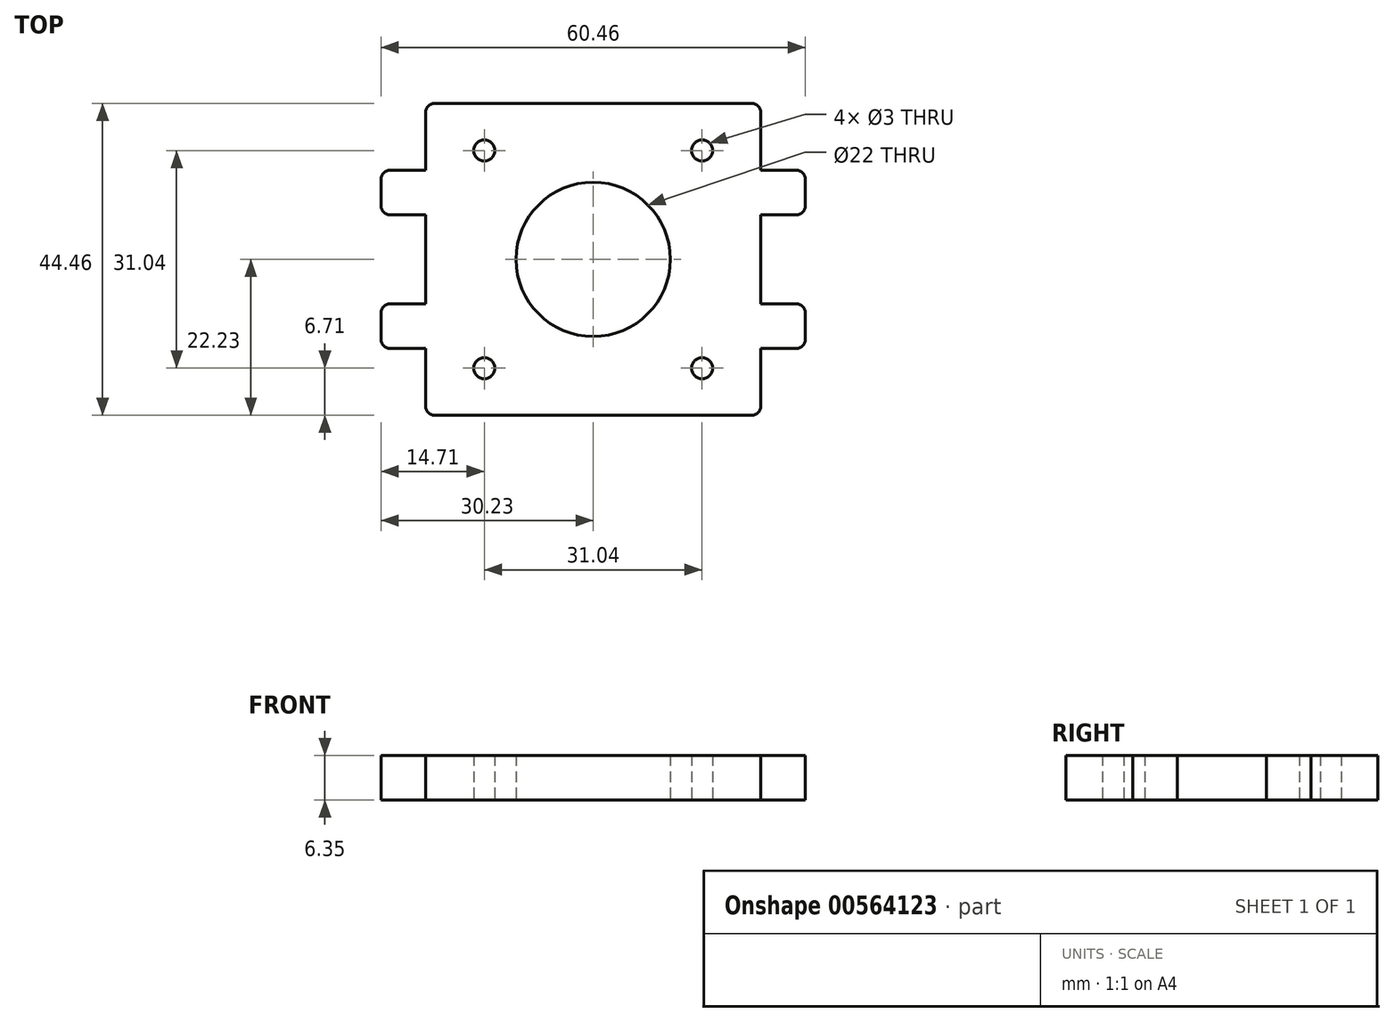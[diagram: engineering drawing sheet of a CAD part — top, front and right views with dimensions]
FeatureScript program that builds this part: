
annotation { "Feature Type Name" : "Feature", "Feature Type Description" : "" }
export const myFeature = defineFeature(function(context is Context, id is Id, definition is map)
    precondition{}
    {
        {
            var Q0;
            Q0=qCreatedBy(makeId("Top.planeOp"),FACE);
            var sketch = newSketch(context, id + "F0", { "sketchPlane" : qUnion([Q0])});
            skLineSegment(sketch, "E0.bottom", {"start": v(-23.88, 22.22) * mm, "end": v(23.88, 22.23) * mm});
            skLineSegment(sketch, "E0.top", {"start": v(-23.88, -22.23) * mm, "end": v(23.88, -22.22) * mm});
            skLineSegment(sketch, "E0.left", {"start": v(-23.88, 22.22) * mm, "end": v(-23.88, -22.23) * mm});
            skLineSegment(sketch, "E0.right", {"start": v(23.88, 22.23) * mm, "end": v(23.88, -22.22) * mm});
            skPoint(sketch, "E0.middle", {"position": v(0, 0) * mm});
            skLineSegment(sketch, "E1", {"start": v(0, 5.5) * mm, "end": v(0, -5.9) * mm});
            skLineSegment(sketch, "E2", {"start": v(-5.75, 0) * mm, "end": v(7.69, 0) * mm});
            skCircle(sketch, "E3", {"center": v(-15.52, 15.52) * mm, "radius": 1.5 * mm});
            skCircle(sketch, "E4.MirrorC", {"center": v(15.52, 15.52) * mm, "radius": 1.5 * mm});
            skCircle(sketch, "E5.MirrorC", {"center": v(-15.52, -15.52) * mm, "radius": 1.5 * mm});
            skCircle(sketch, "E6.MirrorC", {"center": v(15.52, -15.52) * mm, "radius": 1.5 * mm});
            skCircle(sketch, "E7", {"center": v(0, 0) * mm, "radius": 11 * mm});
            skLineSegment(sketch, "E8", {"start": v(-23.88, 12.7) * mm, "end": v(-30.23, 12.7) * mm});
            skLineSegment(sketch, "E9", {"start": v(-30.23, 12.7) * mm, "end": v(-30.23, 6.35) * mm});
            skLineSegment(sketch, "E10", {"start": v(-30.23, 6.35) * mm, "end": v(-23.88, 6.35) * mm});
            skLineSegment(sketch, "E11.MirrorCS", {"start": v(30.23, 6.35) * mm, "end": v(23.88, 6.35) * mm});
            skLineSegment(sketch, "E12.MirrorCS", {"start": v(23.88, 12.7) * mm, "end": v(30.23, 12.7) * mm});
            skLineSegment(sketch, "E13.MirrorCS", {"start": v(30.23, 12.7) * mm, "end": v(30.23, 6.35) * mm});
            skLineSegment(sketch, "E14.MirrorCS", {"start": v(-30.23, -6.35) * mm, "end": v(-23.88, -6.35) * mm});
            skLineSegment(sketch, "E15.MirrorCS", {"start": v(-23.88, -12.7) * mm, "end": v(-30.23, -12.7) * mm});
            skLineSegment(sketch, "E16.MirrorCS", {"start": v(-30.23, -12.7) * mm, "end": v(-30.23, -6.35) * mm});
            skLineSegment(sketch, "E17.MirrorCS", {"start": v(30.23, -6.35) * mm, "end": v(23.88, -6.35) * mm});
            skLineSegment(sketch, "E18.MirrorCS", {"start": v(23.88, -12.7) * mm, "end": v(30.23, -12.7) * mm});
            skLineSegment(sketch, "E19.MirrorCS", {"start": v(30.23, -12.7) * mm, "end": v(30.23, -6.35) * mm});
            skPoint(sketch, "E20", {"position": v(-30.23, -9.53) * mm});
            skPoint(sketch, "E21", {"position": v(-30.23, 9.53) * mm});
            skSolve(sketch);
        }
        {
            var Q0;
            Q0 = qSketchRegion(id + "F0", true);
            extrude(context, id + "F1", {"entities" : qUnion([Q0]), "depth" : 6.35 * mm, "offsetDistance" : 25.4 * mm});
        }
        {
            var Q0;
            Q0=makeQuery(id+"F1.opExtrude","SWEPT_EDGE",EDGE,{"disambiguationData":[OSD([sQuery(id+"F0.wireOp",EDGE,"E0.top"),sQuery(id+"F0.wireOp",EDGE,"E0.left")])]});
            var Q1;
            Q1=makeQuery(id+"F1.opExtrude","SWEPT_EDGE",EDGE,{"disambiguationData":[OSD([sQuery(id+"F0.wireOp",EDGE,"E0.top"),sQuery(id+"F0.wireOp",EDGE,"E0.right")])]});
            var Q2;
            Q2=makeQuery(id+"F1.opExtrude","SWEPT_EDGE",EDGE,{"disambiguationData":[OSD([sQuery(id+"F0.wireOp",EDGE,"E0.bottom"),sQuery(id+"F0.wireOp",EDGE,"E0.right")])]});
            var Q3;
            Q3=makeQuery(id+"F1.opExtrude","SWEPT_EDGE",EDGE,{"disambiguationData":[OSD([sQuery(id+"F0.wireOp",EDGE,"E0.bottom"),sQuery(id+"F0.wireOp",EDGE,"E0.left")])]});
            var Q4;
            Q4=makeQuery(id+"F1.opExtrude","SWEPT_EDGE",EDGE,{"disambiguationData":[OSD([sQuery(id+"F0.wireOp",EDGE,"E18.MirrorCS"),sQuery(id+"F0.wireOp",EDGE,"E19.MirrorCS")])]});
            var Q5;
            Q5=makeQuery(id+"F1.opExtrude","SWEPT_EDGE",EDGE,{"disambiguationData":[OSD([sQuery(id+"F0.wireOp",EDGE,"E17.MirrorCS"),sQuery(id+"F0.wireOp",EDGE,"E19.MirrorCS")])]});
            var Q6;
            Q6=makeQuery(id+"F1.opExtrude","SWEPT_EDGE",EDGE,{"disambiguationData":[OSD([sQuery(id+"F0.wireOp",EDGE,"E11.MirrorCS"),sQuery(id+"F0.wireOp",EDGE,"E13.MirrorCS")])]});
            var Q7;
            Q7=makeQuery(id+"F1.opExtrude","SWEPT_EDGE",EDGE,{"disambiguationData":[OSD([sQuery(id+"F0.wireOp",EDGE,"E12.MirrorCS"),sQuery(id+"F0.wireOp",EDGE,"E13.MirrorCS")])]});
            var Q8;
            Q8=makeQuery(id+"F1.opExtrude","SWEPT_EDGE",EDGE,{"disambiguationData":[OSD([sQuery(id+"F0.wireOp",EDGE,"E8"),sQuery(id+"F0.wireOp",EDGE,"E9")])]});
            var Q9;
            Q9=makeQuery(id+"F1.opExtrude","SWEPT_EDGE",EDGE,{"disambiguationData":[OSD([sQuery(id+"F0.wireOp",EDGE,"E9"),sQuery(id+"F0.wireOp",EDGE,"E10")])]});
            var Q10;
            Q10=makeQuery(id+"F1.opExtrude","SWEPT_EDGE",EDGE,{"disambiguationData":[OSD([sQuery(id+"F0.wireOp",EDGE,"E14.MirrorCS"),sQuery(id+"F0.wireOp",EDGE,"E16.MirrorCS")])]});
            var Q11;
            Q11=makeQuery(id+"F1.opExtrude","SWEPT_EDGE",EDGE,{"disambiguationData":[OSD([sQuery(id+"F0.wireOp",EDGE,"E15.MirrorCS"),sQuery(id+"F0.wireOp",EDGE,"E16.MirrorCS")])]});
            fillet(context, id + "F2", {"entities" : qUnion([Q0, Q1, Q2, Q3, Q4, Q5, Q6, Q7, Q8, Q9, Q10, Q11]), "radius" : 1.27 * mm, "tangentPropagation" : true, "allowEdgeOverflow" : false});
        }
    });
